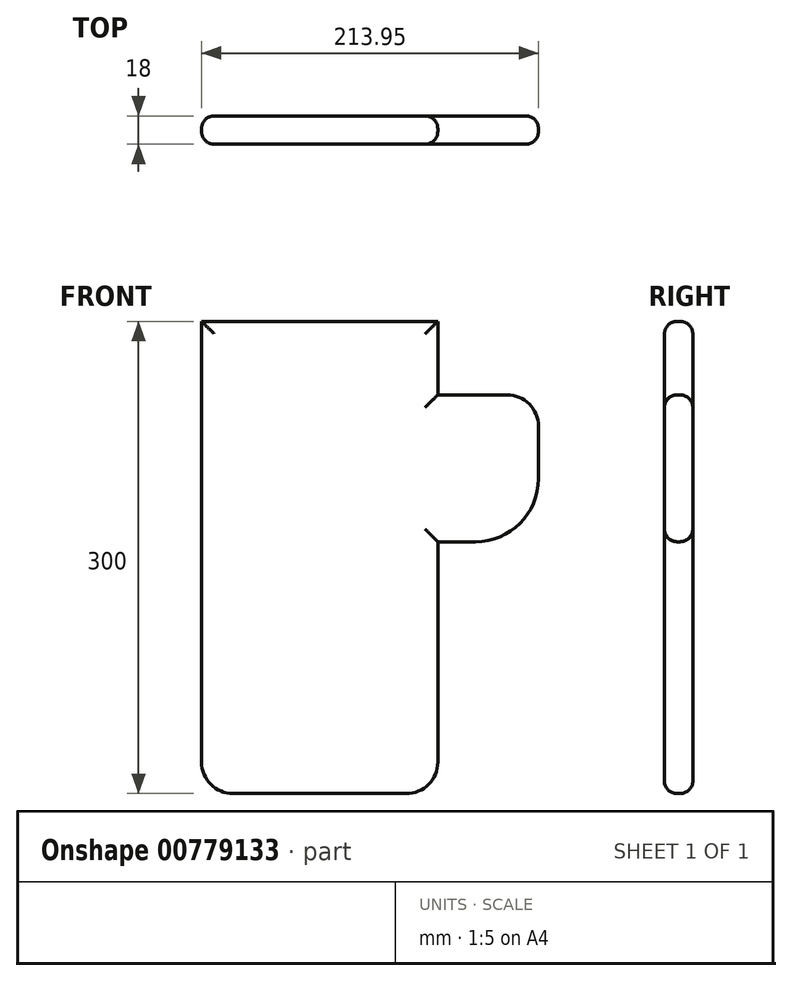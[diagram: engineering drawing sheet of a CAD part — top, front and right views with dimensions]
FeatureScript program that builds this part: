
annotation { "Feature Type Name" : "Feature", "Feature Type Description" : "" }
export const myFeature = defineFeature(function(context is Context, id is Id, definition is map)
    precondition{}
    {
        {
            var Q0;
            Q0=qCreatedBy(makeId("Front.planeOp"),FACE);
            var sketch = newSketch(context, id + "F0", { "sketchPlane" : qUnion([Q0])});
            skLineSegment(sketch, "E0.bottom", {"start": v(-37.71, -208.99) * mm, "end": v(72.29, -208.99) * mm});
            skLineSegment(sketch, "E0.top", {"start": v(-57.71, 91.01) * mm, "end": v(92.29, 91.01) * mm});
            skLineSegment(sketch, "E0.left", {"start": v(-57.71, -188.99) * mm, "end": v(-57.71, 91.01) * mm});
            skLineSegment(sketch, "E0.right", {"start": v(92.29, -188.99) * mm, "end": v(92.29, 91.01) * mm});
            skPoint(sketch, "E1.visualSharp", {"position": v(92.29, -208.99) * mm});
            skArc(sketch, "E1.filletArc", {"start": v(72.29, -208.99) * mm, "mid": v(86.43, -203.13) * mm, "end": v(92.29, -188.99) * mm});
            skPoint(sketch, "E2.visualSharp", {"position": v(-57.71, -208.99) * mm});
            skArc(sketch, "E2.filletArc", {"start": v(-57.71, -188.99) * mm, "mid": v(-51.85, -203.13) * mm, "end": v(-37.71, -208.99) * mm});
            skLineSegment(sketch, "E3.bottom", {"start": v(92.29, -48.99) * mm, "end": v(116.24, -48.99) * mm});
            skLineSegment(sketch, "E3.top", {"start": v(92.29, 44.3) * mm, "end": v(136.24, 44.3) * mm});
            skLineSegment(sketch, "E3.left", {"start": v(92.29, -48.99) * mm, "end": v(92.29, 44.3) * mm});
            skLineSegment(sketch, "E3.right", {"start": v(156.24, -8.99) * mm, "end": v(156.24, 24.3) * mm});
            skPoint(sketch, "E4.visualSharp", {"position": v(156.24, 44.3) * mm});
            skArc(sketch, "E4.filletArc", {"start": v(156.24, 24.3) * mm, "mid": v(150.38, 38.44) * mm, "end": v(136.24, 44.3) * mm});
            skArc(sketch, "E5.filletArc", {"start": v(116.24, -48.99) * mm, "mid": v(144.52, -37.27) * mm, "end": v(156.24, -8.99) * mm});
            skSolve(sketch);
        }
        {
            var Q0;
            Q0 = qSketchRegion(id + "F0", true);
            extrude(context, id + "F1", {"entities" : qUnion([Q0]), "depth" : 18 * mm, "offsetDistance" : 25 * mm});
        }
        {
            var Q0;
            Q0=makeQuery(id+"F1.opExtrude","CAP_EDGE",EDGE,{"disambiguationData":[OSD([sQuery(id+"F0.wireOp",EDGE,"E0.left")])],"isStart":false});
            var Q1;
            Q1=makeQuery(id+"F1.opExtrude","CAP_EDGE",EDGE,{"disambiguationData":[OSD([sQuery(id+"F0.wireOp",EDGE,"E0.left")])],"isStart":true});
            var Q2;
            Q2=makeQuery(id+"F1.opExtrude","CAP_EDGE",EDGE,{"disambiguationData":[OSD([sQuery(id+"F0.wireOp",EDGE,"E0.top")])],"isStart":false});
            var Q3;
            Q3=makeQuery(id+"F1.opExtrude","CAP_EDGE",EDGE,{"disambiguationData":[OSD([sQuery(id+"F0.wireOp",EDGE,"E0.top")])],"isStart":true});
            var Q4;
            {var subQ0=sQuery(id+"F0.wireOp",EDGE,"E0.right");Q4=makeQuery(id+"F1.opExtrude","CAP_EDGE",EDGE,{"disambiguationData":[OSD([subQ0]),TDD([makeQuery(id+"F0.imprint","IMPRINT",EDGE,{"disambiguationData":[TD([[makeQuery(id+"F0.imprint","INTERSECT",VERTEX,{"derivedFrom":[sQuery(id+"F0.wireOp",EDGE,"E0.top"),subQ0]}),1.0]])],"derivedFrom":subQ0})])],"isStart":false});}
            var Q5;
            {var subQ0=sQuery(id+"F0.wireOp",EDGE,"E0.right");Q5=makeQuery(id+"F1.opExtrude","CAP_EDGE",EDGE,{"disambiguationData":[OSD([subQ0]),TDD([makeQuery(id+"F0.imprint","IMPRINT",EDGE,{"disambiguationData":[TD([[makeQuery(id+"F0.imprint","INTERSECT",VERTEX,{"derivedFrom":[sQuery(id+"F0.wireOp",EDGE,"E0.top"),subQ0]}),1.0]])],"derivedFrom":subQ0})])],"isStart":true});}
            var Q6;
            Q6=makeQuery(id+"F1.opExtrude","CAP_EDGE",EDGE,{"disambiguationData":[OSD([sQuery(id+"F0.wireOp",EDGE,"E3.top")])],"isStart":true});
            var Q7;
            Q7=makeQuery(id+"F1.opExtrude","CAP_EDGE",EDGE,{"disambiguationData":[OSD([sQuery(id+"F0.wireOp",EDGE,"E3.top")])],"isStart":false});
            var Q8;
            Q8=makeQuery(id+"F1.opExtrude","CAP_EDGE",EDGE,{"disambiguationData":[OSD([sQuery(id+"F0.wireOp",EDGE,"E4.filletArc")])],"isStart":true});
            fillet(context, id + "F2", {"entities" : qUnion([Q0, Q1, Q2, Q3, Q4, Q5, Q6, Q7, Q8]), "radius" : 8 * mm, "tangentPropagation" : true, "allowEdgeOverflow" : false});
        }
        {
            var Q0;
            Q0=makeQuery(id+"F1.opExtrude","SWEPT_BODY",BODY,{"disambiguationData":[OSD([sQuery(id+"F0.wireOp",EDGE,"E0.bottom"),sQuery(id+"F0.wireOp",EDGE,"E0.top"),sQuery(id+"F0.wireOp",EDGE,"E0.left"),sQuery(id+"F0.wireOp",EDGE,"E0.right"),sQuery(id+"F0.wireOp",EDGE,"E1.filletArc"),sQuery(id+"F0.wireOp",EDGE,"E2.filletArc"),sQuery(id+"F0.wireOp",EDGE,"E3.bottom"),sQuery(id+"F0.wireOp",EDGE,"E3.top"),sQuery(id+"F0.wireOp",EDGE,"E3.right"),sQuery(id+"F0.wireOp",EDGE,"E4.filletArc"),sQuery(id+"F0.wireOp",EDGE,"E5.filletArc"),sQuery(id+"F0.wireOp",EDGE,"597f47ed-a96c-4448-bff0-88619b2691ce.sketch_text.stroke-0"),sQuery(id+"F0.wireOp",EDGE,"597f47ed-a96c-4448-bff0-88619b2691ce.sketch_text.stroke-1"),sQuery(id+"F0.wireOp",EDGE,"597f47ed-a96c-4448-bff0-88619b2691ce.sketch_text.stroke-2"),sQuery(id+"F0.wireOp",EDGE,"597f47ed-a96c-4448-bff0-88619b2691ce.sketch_text.stroke-3"),sQuery(id+"F0.wireOp",EDGE,"597f47ed-a96c-4448-bff0-88619b2691ce.sketch_text.stroke-4"),sQuery(id+"F0.wireOp",EDGE,"597f47ed-a96c-4448-bff0-88619b2691ce.sketch_text.stroke-5"),sQuery(id+"F0.wireOp",EDGE,"597f47ed-a96c-4448-bff0-88619b2691ce.sketch_text.stroke-6"),sQuery(id+"F0.wireOp",EDGE,"597f47ed-a96c-4448-bff0-88619b2691ce.sketch_text.stroke-7"),sQuery(id+"F0.wireOp",EDGE,"597f47ed-a96c-4448-bff0-88619b2691ce.sketch_text.stroke-8"),sQuery(id+"F0.wireOp",EDGE,"597f47ed-a96c-4448-bff0-88619b2691ce.sketch_text.stroke-9"),sQuery(id+"F0.wireOp",EDGE,"597f47ed-a96c-4448-bff0-88619b2691ce.sketch_text.stroke-10"),sQuery(id+"F0.wireOp",EDGE,"597f47ed-a96c-4448-bff0-88619b2691ce.sketch_text.stroke-11"),sQuery(id+"F0.wireOp",EDGE,"597f47ed-a96c-4448-bff0-88619b2691ce.sketch_text.stroke-12"),sQuery(id+"F0.wireOp",EDGE,"597f47ed-a96c-4448-bff0-88619b2691ce.sketch_text.stroke-13"),sQuery(id+"F0.wireOp",EDGE,"597f47ed-a96c-4448-bff0-88619b2691ce.sketch_text.stroke-14"),sQuery(id+"F0.wireOp",EDGE,"597f47ed-a96c-4448-bff0-88619b2691ce.sketch_text.stroke-15"),sQuery(id+"F0.wireOp",EDGE,"597f47ed-a96c-4448-bff0-88619b2691ce.sketch_text.stroke-16"),sQuery(id+"F0.wireOp",EDGE,"597f47ed-a96c-4448-bff0-88619b2691ce.sketch_text.stroke-17"),sQuery(id+"F0.wireOp",EDGE,"597f47ed-a96c-4448-bff0-88619b2691ce.sketch_text.stroke-18"),sQuery(id+"F0.wireOp",EDGE,"597f47ed-a96c-4448-bff0-88619b2691ce.sketch_text.stroke-19"),sQuery(id+"F0.wireOp",EDGE,"597f47ed-a96c-4448-bff0-88619b2691ce.sketch_text.stroke-20"),sQuery(id+"F0.wireOp",EDGE,"597f47ed-a96c-4448-bff0-88619b2691ce.sketch_text.stroke-21"),sQuery(id+"F0.wireOp",EDGE,"597f47ed-a96c-4448-bff0-88619b2691ce.sketch_text.stroke-22"),sQuery(id+"F0.wireOp",EDGE,"597f47ed-a96c-4448-bff0-88619b2691ce.sketch_text.stroke-23"),sQuery(id+"F0.wireOp",EDGE,"597f47ed-a96c-4448-bff0-88619b2691ce.sketch_text.stroke-24"),sQuery(id+"F0.wireOp",EDGE,"597f47ed-a96c-4448-bff0-88619b2691ce.sketch_text.stroke-25"),sQuery(id+"F0.wireOp",EDGE,"597f47ed-a96c-4448-bff0-88619b2691ce.sketch_text.stroke-26"),sQuery(id+"F0.wireOp",EDGE,"597f47ed-a96c-4448-bff0-88619b2691ce.sketch_text.stroke-27"),sQuery(id+"F0.wireOp",EDGE,"597f47ed-a96c-4448-bff0-88619b2691ce.sketch_text.stroke-28"),sQuery(id+"F0.wireOp",EDGE,"597f47ed-a96c-4448-bff0-88619b2691ce.sketch_text.stroke-29"),sQuery(id+"F0.wireOp",EDGE,"597f47ed-a96c-4448-bff0-88619b2691ce.sketch_text.stroke-30"),sQuery(id+"F0.wireOp",EDGE,"597f47ed-a96c-4448-bff0-88619b2691ce.sketch_text.stroke-31"),sQuery(id+"F0.wireOp",EDGE,"597f47ed-a96c-4448-bff0-88619b2691ce.sketch_text.stroke-32"),sQuery(id+"F0.wireOp",EDGE,"597f47ed-a96c-4448-bff0-88619b2691ce.sketch_text.stroke-38"),sQuery(id+"F0.wireOp",EDGE,"597f47ed-a96c-4448-bff0-88619b2691ce.sketch_text.stroke-39"),sQuery(id+"F0.wireOp",EDGE,"597f47ed-a96c-4448-bff0-88619b2691ce.sketch_text.stroke-40"),sQuery(id+"F0.wireOp",EDGE,"597f47ed-a96c-4448-bff0-88619b2691ce.sketch_text.stroke-41"),sQuery(id+"F0.wireOp",EDGE,"597f47ed-a96c-4448-bff0-88619b2691ce.sketch_text.stroke-42"),sQuery(id+"F0.wireOp",EDGE,"597f47ed-a96c-4448-bff0-88619b2691ce.sketch_text.stroke-43"),sQuery(id+"F0.wireOp",EDGE,"597f47ed-a96c-4448-bff0-88619b2691ce.sketch_text.stroke-44"),sQuery(id+"F0.wireOp",EDGE,"597f47ed-a96c-4448-bff0-88619b2691ce.sketch_text.stroke-45"),sQuery(id+"F0.wireOp",EDGE,"597f47ed-a96c-4448-bff0-88619b2691ce.sketch_text.stroke-46"),sQuery(id+"F0.wireOp",EDGE,"597f47ed-a96c-4448-bff0-88619b2691ce.sketch_text.stroke-47"),sQuery(id+"F0.wireOp",EDGE,"597f47ed-a96c-4448-bff0-88619b2691ce.sketch_text.stroke-48"),sQuery(id+"F0.wireOp",EDGE,"597f47ed-a96c-4448-bff0-88619b2691ce.sketch_text.stroke-49"),sQuery(id+"F0.wireOp",EDGE,"597f47ed-a96c-4448-bff0-88619b2691ce.sketch_text.stroke-50"),sQuery(id+"F0.wireOp",EDGE,"597f47ed-a96c-4448-bff0-88619b2691ce.sketch_text.stroke-51"),sQuery(id+"F0.wireOp",EDGE,"597f47ed-a96c-4448-bff0-88619b2691ce.sketch_text.stroke-52"),sQuery(id+"F0.wireOp",EDGE,"597f47ed-a96c-4448-bff0-88619b2691ce.sketch_text.stroke-53"),sQuery(id+"F0.wireOp",EDGE,"597f47ed-a96c-4448-bff0-88619b2691ce.sketch_text.stroke-54"),sQuery(id+"F0.wireOp",EDGE,"597f47ed-a96c-4448-bff0-88619b2691ce.sketch_text.stroke-55"),sQuery(id+"F0.wireOp",EDGE,"597f47ed-a96c-4448-bff0-88619b2691ce.sketch_text.stroke-56"),sQuery(id+"F0.wireOp",EDGE,"597f47ed-a96c-4448-bff0-88619b2691ce.sketch_text.stroke-57"),sQuery(id+"F0.wireOp",EDGE,"597f47ed-a96c-4448-bff0-88619b2691ce.sketch_text.stroke-58"),sQuery(id+"F0.wireOp",EDGE,"597f47ed-a96c-4448-bff0-88619b2691ce.sketch_text.stroke-59"),sQuery(id+"F0.wireOp",EDGE,"597f47ed-a96c-4448-bff0-88619b2691ce.sketch_text.stroke-60"),sQuery(id+"F0.wireOp",EDGE,"597f47ed-a96c-4448-bff0-88619b2691ce.sketch_text.stroke-61"),sQuery(id+"F0.wireOp",EDGE,"597f47ed-a96c-4448-bff0-88619b2691ce.sketch_text.stroke-62"),sQuery(id+"F0.wireOp",EDGE,"597f47ed-a96c-4448-bff0-88619b2691ce.sketch_text.stroke-63"),sQuery(id+"F0.wireOp",EDGE,"597f47ed-a96c-4448-bff0-88619b2691ce.sketch_text.stroke-64"),sQuery(id+"F0.wireOp",EDGE,"597f47ed-a96c-4448-bff0-88619b2691ce.sketch_text.stroke-65"),sQuery(id+"F0.wireOp",EDGE,"597f47ed-a96c-4448-bff0-88619b2691ce.sketch_text.stroke-66"),sQuery(id+"F0.wireOp",EDGE,"597f47ed-a96c-4448-bff0-88619b2691ce.sketch_text.stroke-67"),sQuery(id+"F0.wireOp",EDGE,"597f47ed-a96c-4448-bff0-88619b2691ce.sketch_text.stroke-68")])]});
            transform(context, id + "F3", {"entities" : qUnion([Q0]), "transformType" : TransformType.TRANSLATION_3D, "dx" : 5 * mm, "dy" : 0 * mm, "dz" : 0 * mm, "makeCopy" : false});
        }
    });
